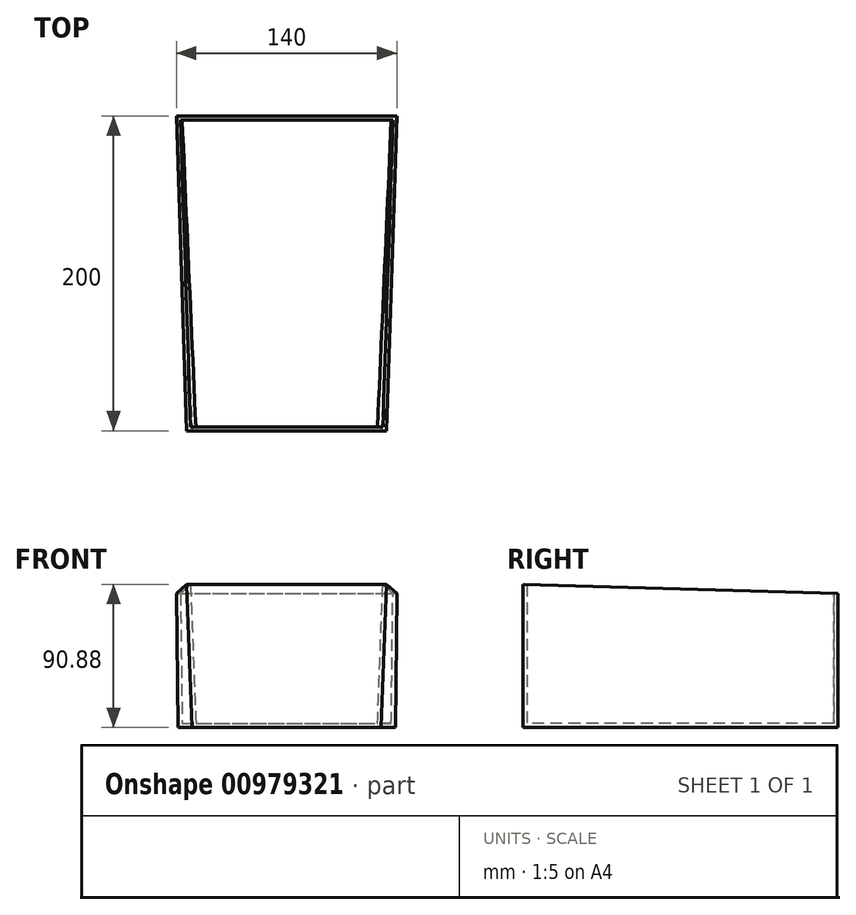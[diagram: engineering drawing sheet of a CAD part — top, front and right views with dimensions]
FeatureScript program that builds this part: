
annotation { "Feature Type Name" : "Feature", "Feature Type Description" : "" }
export const myFeature = defineFeature(function(context is Context, id is Id, definition is map)
    precondition{}
    {
        {
            var Q0;
            Q0=qCreatedBy(makeId("Front.planeOp"),FACE);
            var sketch = newSketch(context, id + "F0", { "sketchPlane" : qUnion([Q0])});
            skLineSegment(sketch, "E0", {"start": v(0, 0) * mm, "end": v(0, 95) * mm, "construction": true});
            skLineSegment(sketch, "E1", {"start": v(0, 0) * mm, "end": v(70, 0) * mm, "construction": true});
            skLineSegment(sketch, "E2", {"start": v(0, 0) * mm, "end": v(0, 85) * mm});
            skLineSegment(sketch, "E3", {"start": v(0, 85) * mm, "end": v(70, 85) * mm});
            skLineSegment(sketch, "E4", {"start": v(70, 85) * mm, "end": v(69, 0) * mm});
            skLineSegment(sketch, "E5", {"start": v(69, 0) * mm, "end": v(0, 0) * mm});
            skLineSegment(sketch, "E6.MirrorCS", {"start": v(-69, 0) * mm, "end": v(0, 0) * mm});
            skLineSegment(sketch, "E7.MirrorCS", {"start": v(0, 0) * mm, "end": v(-70, 0) * mm, "construction": true});
            skLineSegment(sketch, "E8.MirrorCS", {"start": v(0, 85) * mm, "end": v(-70, 85) * mm});
            skLineSegment(sketch, "E9.MirrorCS", {"start": v(-70, 85) * mm, "end": v(-69, 0) * mm});
            skSolve(sketch);
        }
        {
            var Q0;
            Q0=qCreatedBy(makeId("Top.planeOp"),FACE);
            var sketch = newSketch(context, id + "F1", { "sketchPlane" : qUnion([Q0])});
            skLineSegment(sketch, "E10", {"start": v(0, 0) * mm, "end": v(0, -200) * mm, "construction": true});
            skSolve(sketch);
        }
        {
            var Q0;
            Q0=sQuery(id+"F1.wireOp",VERTEX,"E10.end");
            var Q1;
            Q1=qCreatedBy(makeId("Front.planeOp"),FACE);
            cPlane(context, id + "F2", {"entities" : qUnion([Q0, Q1]), "cplaneType" : CPlaneType.PLANE_POINT, "offset" : 25 * mm, "width" : 150 * mm, "height" : 150 * mm});
        }
        {
            var Q0;
            Q0=qCreatedBy(id+"F2.planeOp",FACE);
            var sketch = newSketch(context, id + "F3", { "sketchPlane" : qUnion([Q0])});
            skLineSegment(sketch, "E11", {"start": v(0, 0) * mm, "end": v(60, 0) * mm});
            skLineSegment(sketch, "E12", {"start": v(60, 0) * mm, "end": v(63.5, 90.88) * mm});
            skLineSegment(sketch, "E13", {"start": v(63.5, 90.88) * mm, "end": v(0, 90.88) * mm});
            skLineSegment(sketch, "E14.MirrorCS", {"start": v(-63.5, 90.88) * mm, "end": v(0, 90.88) * mm});
            skLineSegment(sketch, "E15.MirrorCS", {"start": v(-60, 0) * mm, "end": v(-63.5, 90.88) * mm});
            skLineSegment(sketch, "E16.MirrorCS", {"start": v(0, 0) * mm, "end": v(-60, 0) * mm});
            skSolve(sketch);
        }
        {
            var Q0;
            Q0 = qSketchRegion(id + "F0", true);
            var Q1;
            Q1 = qSketchRegion(id + "F3", true);
            loft(context, id + "F4", {"sheetProfilesArray" : [{ "sheetProfileEntities" : qUnion([Q0]) }, { "sheetProfileEntities" : qUnion([Q1]) }]});
        }
        {
            var Q0;
            Q0=makeQuery(id+"F4.opLoft","SWEPT_FACE",FACE,{"disambiguationData":[OSD([sQuery(id+"F0.wireOp",EDGE,"E2"),sQuery(id+"F0.wireOp",EDGE,"E3"),sQuery(id+"F0.wireOp",EDGE,"E4"),sQuery(id+"F0.wireOp",EDGE,"E8.MirrorCS"),sQuery(id+"F0.wireOp",EDGE,"E9.MirrorCS"),sQuery(id+"F3.wireOp",EDGE,"E12"),sQuery(id+"F3.wireOp",EDGE,"E13"),sQuery(id+"F3.wireOp",EDGE,"E14.MirrorCS"),sQuery(id+"F3.wireOp",EDGE,"E15.MirrorCS")])]});
            shell(context, id + "F5", {"entities" : qUnion([Q0]), "thickness" : 2.5 * mm});
        }
    });
